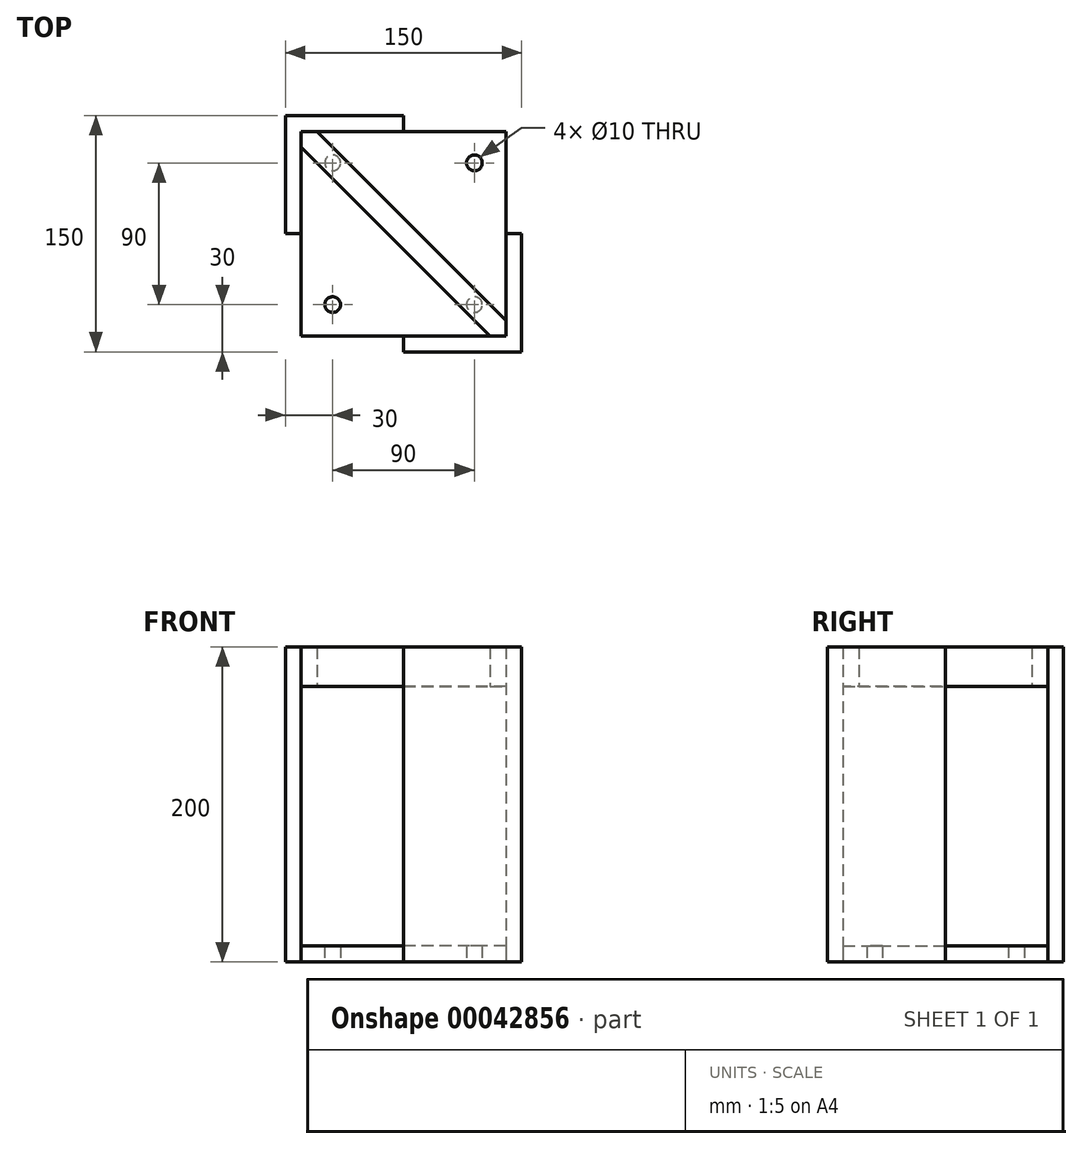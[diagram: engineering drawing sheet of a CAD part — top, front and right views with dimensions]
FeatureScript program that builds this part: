
annotation { "Feature Type Name" : "Feature", "Feature Type Description" : "" }
export const myFeature = defineFeature(function(context is Context, id is Id, definition is map)
    precondition{}
    {
        {
            var Q0;
            Q0=qCreatedBy(makeId("Top.planeOp"),FACE);
            var sketch = newSketch(context, id + "F0", { "sketchPlane" : qUnion([Q0])});
            skLineSegment(sketch, "E0.rect.bottom", {"start": v(65, -65) * mm, "end": v(-65, -65) * mm});
            skLineSegment(sketch, "E0.rect.top", {"start": v(65, 65) * mm, "end": v(-65, 65) * mm});
            skLineSegment(sketch, "E0.rect.left", {"start": v(65, -65) * mm, "end": v(65, 65) * mm});
            skLineSegment(sketch, "E0.rect.right", {"start": v(-65, -65) * mm, "end": v(-65, 65) * mm});
            skPoint(sketch, "E0.rect.middle", {"position": v(0, 0) * mm});
            skCircle(sketch, "E1", {"center": v(-45, -45) * mm, "radius": 5 * mm});
            skCircle(sketch, "E2.0.1.0", {"center": v(-45, 45) * mm, "radius": 5 * mm});
            skCircle(sketch, "E2.1.0.0", {"center": v(45, -45) * mm, "radius": 5 * mm});
            skCircle(sketch, "E2.1.1.0", {"center": v(45, 45) * mm, "radius": 5 * mm});
            skLineSegment(sketch, "E2.direction1", {"start": v(-45, -45) * mm, "end": v(45, -45) * mm, "construction": true});
            skLineSegment(sketch, "E2.direction2", {"start": v(-45, -45) * mm, "end": v(-45, 45) * mm, "construction": true});
            skLineSegment(sketch, "E3", {"start": v(-75, 0) * mm, "end": v(-75, 75) * mm});
            skLineSegment(sketch, "E4", {"start": v(-75, 75) * mm, "end": v(0, 75) * mm});
            skLineSegment(sketch, "E5", {"start": v(0, 75) * mm, "end": v(0, 65) * mm});
            skLineSegment(sketch, "E6", {"start": v(0, 65) * mm, "end": v(-65, 65) * mm});
            skLineSegment(sketch, "E7.MirrorCS", {"start": v(-65, 0) * mm, "end": v(-75, 0) * mm});
            skLineSegment(sketch, "E8", {"start": v(-65, -65) * mm, "end": v(65, 65) * mm, "construction": true});
            skLineSegment(sketch, "E9.MirrorCS", {"start": v(75, 0) * mm, "end": v(65, 0) * mm});
            skLineSegment(sketch, "E10.MirrorCS", {"start": v(75, -75) * mm, "end": v(75, 0) * mm});
            skLineSegment(sketch, "E11.MirrorCS", {"start": v(0, -75) * mm, "end": v(75, -75) * mm});
            skLineSegment(sketch, "E12.MirrorCS", {"start": v(0, -65) * mm, "end": v(0, -75) * mm});
            skSolve(sketch);
        }
        {
            var Q0;
            Q0=makeQuery(id+"F0.imprint","IMPRINT",FACE,{"disambiguationData":[TD([[makeQuery(id+"F0.imprint","IMPRINT",EDGE,{"derivedFrom":sQuery(id+"F0.wireOp",EDGE,"E3")}),-1.0]])]});
            var Q1;
            {var subQ4=sQuery(id+"F0.wireOp",EDGE,"E9.MirrorCS");Q1=makeQuery(id+"F0.imprint","IMPRINT",FACE,{"disambiguationData":[TD([[makeQuery(id+"F0.imprint","IMPRINT",EDGE,{"derivedFrom":subQ4}),1.0]])]});}
            extrude(context, id + "F1", {"entities" : qUnion([Q0, Q1]), "depth" : 200 * mm});
        }
        {
            var Q0;
            {var subQ5=sQuery(id+"F0.wireOp",EDGE,"E0.rect.top");Q0=makeQuery(id+"F0.imprint","IMPRINT",FACE,{"disambiguationData":[TD([[makeQuery(id+"F0.imprint","IMPRINT",EDGE,{"derivedFrom":subQ5}),1.0]])]});}
            extrude(context, id + "F2", {"entities" : qUnion([Q0]), "depth" : 10 * mm});
        }
        {
            var Q0;
            Q0=qCreatedBy(makeId("Top.planeOp"),FACE);
            var sketch = newSketch(context, id + "F3", { "sketchPlane" : qUnion([Q0])});
            skLineSegment(sketch, "E13", {"start": v(-65, 65) * mm, "end": v(-65, 55) * mm});
            skLineSegment(sketch, "E14", {"start": v(-65, 55) * mm, "end": v(55, -65) * mm});
            skLineSegment(sketch, "E15", {"start": v(55, -65) * mm, "end": v(65, -65) * mm});
            skLineSegment(sketch, "E16", {"start": v(65, -65) * mm, "end": v(65, -55) * mm});
            skLineSegment(sketch, "E17", {"start": v(65, -55) * mm, "end": v(-55, 65) * mm});
            skLineSegment(sketch, "E18", {"start": v(-55, 65) * mm, "end": v(-65, 65) * mm});
            skSolve(sketch);
        }
        {
            var Q0;
            Q0 = qSketchRegion(id + "F3", true);
            extrude(context, id + "F4", {"entities" : qUnion([Q0]), "depth" : 25 * mm});
        }
        {
            var Q0;
            Q0=makeQuery(id+"F4.opExtrude","SWEPT_BODY",BODY,{"disambiguationData":[OSD([sQuery(id+"F3.wireOp",EDGE,"E13"),sQuery(id+"F3.wireOp",EDGE,"E14"),sQuery(id+"F3.wireOp",EDGE,"E15"),sQuery(id+"F3.wireOp",EDGE,"E16"),sQuery(id+"F3.wireOp",EDGE,"E17"),sQuery(id+"F3.wireOp",EDGE,"E18")])]});
            var Q1;
            Q1=makeQuery(id+"F4.opExtrude","CAP_VERTEX",VERTEX,{"disambiguationData":[OSD([sQuery(id+"F3.wireOp",EDGE,"E13"),sQuery(id+"F3.wireOp",EDGE,"E18")])],"isStart":false});
            var Q2;
            Q2=makeQuery(id+"F1.opExtrude","CAP_VERTEX",VERTEX,{"disambiguationData":[OSD([sQuery(id+"F0.wireOp",EDGE,"E0.rect.right"),sQuery(id+"F0.wireOp",EDGE,"E6")])],"isStart":false});
            transform(context, id + "F5", {"entities" : qUnion([Q0]), "transformType" : TransformType.TRANSLATION_ENTITY, "oppositeDirectionEntity" : false, "transformLine" : qUnion([Q1, Q2]), "makeCopy" : false});
        }
    });
